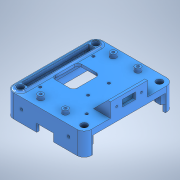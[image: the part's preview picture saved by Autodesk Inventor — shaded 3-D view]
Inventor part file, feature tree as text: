
AUTODESK INVENTOR PART (.ipt)
format: ipt  version: 2022 (Build 260153000, 153)  size: 752,640 bytes
history: native  units: mm
features: sketch x26, extrude x21, mirror x8, fillet x7, hole x5, plane x5
ambient origin geometry x8: Origin, YZ Plane, XZ Plane, XY Plane, X Axis, Y Axis, Z Axis, Center Point
bodies: Solid1 (feature_tree)
feature tree (72):
  extrude  "Extrusion1"  Depth=6.2mm
  extrude  "Extrusion2"  Depth=49.0mm
  extrude  "Extrusion3"  Depth=58.0mm
  extrude  "Extrusion4"  Depth=58.0mm
  extrude  "Extrusion5"  Depth=7.0mm
  hole  "Hole1"  [1 undecoded]
  extrude  "Extrusion6"  Depth=2.0mm TaperAngle=0.0deg
  extrude  "Extrusion8"  Depth=5.0mm
  extrude  "Extrusion12"  Depth=6.5mm
  extrude  "Extrusion13"  Depth=5.0mm
  extrude  "Extrusion14"  Depth=5.0mm TaperAngle=0.0deg
  extrude  "Extrusion15"  Depth=7.0mm
  fillet  "Fillet1"  Radius=17.0mm
  hole  "Hole2"  [1 undecoded]
  extrude  "Extrusion16"  Depth=2.0mm
  extrude  "Extrusion17"  Depth=9.525mm
  hole  "Hole3"  [1 undecoded]
  extrude  "Extrusion18"  Depth=3.0mm TaperAngle=0.0deg
  extrude  "Extrusion19"  Depth=11.0mm
  mirror  "Mirror4"
  extrude  "Extrusion20"  Depth=11.0mm
  hole  "Hole4"  [1 undecoded]
  plane  "Work Plane3"
  mirror  "Mirror5"
  hole  "Hole5"  [1 undecoded]
  extrude  "Extrusion21"  Depth=13.0mm
  plane  "Work Plane4"
  plane  "Work Plane5"
  mirror  "Mirror6"
  mirror  "Mirror7"
  fillet  "Fillet2"  Radius=6.0mm
  fillet  "Fillet3"  Radius=18.0mm
  extrude  "Extrusion22"  Depth=13.0mm
  fillet  "Fillet4"  Radius=13.0mm
  extrude  "Extrusion23"  Depth=2.0mm TaperAngle=0.0deg
  mirror  "Mirror8"
  mirror  "Mirror9"
  fillet  "Fillet5"  Radius=7.15mm
  fillet  "Fillet6"  Radius=7.15mm
  fillet  "Fillet7"  Radius=7.15mm
  extrude  "Extrusion24"  Depth=2.0mm TaperAngle=0.0deg
  extrude  "Extrusion25"  Depth=3.1mm
  mirror  "Mirror10"
  mirror  "Mirror11"
  sketch  "Sketch1"  dims[d0=6.2mm d1=6.2mm]
  sketch  "Sketch2"  dims[d2=6.2mm d3=49.0mm]
  sketch  "Sketch4"  dims[d4=58.0mm d5=6.2mm]
  sketch  "Sketch5"  dims[d6=58.0mm d7=49.0mm]
  sketch  "Sketch6"  dims[d8=10.0mm d9=0.0mm d10=7.0mm]
  sketch  "Sketch7"  dims[d11=7.0mm d12=7.0mm]
  sketch  "Sketch8"  dims[d13=7.0mm d14=2.0mm d15=0.0mm]
  sketch  "Sketch12"  dims[d19=1.0mm d20=5.0mm]
  sketch  "Sketch15"  dims[d21=52.0mm d22=6.5mm]
  sketch  "Sketch16"  dims[d23=2.0mm d24=0.0mm d31=5.0mm]
  sketch  "Sketch17"  dims[d32=5.0mm d33=5.0mm d34=0.0mm]
  sketch  "Sketch18"  dims[d35=20.5mm d36=7.0mm d37=17.0mm]
  sketch  "Sketch19"  dims[d39=5.5mm d40=0.0mm d41=16.0mm]
  sketch  "Sketch20"  dims[d42=2.0mm d43=6.0mm d44=4.0mm d45=2.0mm d46=90.0deg d47=8.0mm d48=20.594885mm d49=2.25mm]
  sketch  "Sketch21"  dims[d50=55.88mm d51=9.525mm]
  sketch  "Sketch22"  dims[d52=4.5mm d53=4.5mm]
  sketch  "Sketch23"  dims[d54=4.6mm d55=3.0mm d56=0.0mm]
  sketch  "Sketch24"  dims[d65=11.0mm d66=11.0mm]
  sketch  "Sketch25"  dims[d67=11.0mm d68=11.0mm]
  sketch  "Sketch26"  dims[d69=17.48mm d70=0.0mm d88=13.0mm]
  sketch  "Sketch27"  dims[d89=1.0mm d90=1.0mm]
  sketch  "Sketch28"  dims[d91=2.0mm d92=0.0mm d93=13.0mm d94=6.0mm d95=18.0mm]
  plane  "Work Plane6"
  plane  "Work Plane7"
  sketch  "Sketch29"  dims[d96=2.0mm d97=0.0mm d98=15.0mm d99=13.0mm]
  sketch  "Sketch30"  dims[d100=20.5mm d101=2.0mm d102=0.0mm d103=7.15mm d104=7.15mm d105=7.15mm]
  sketch  "Sketch32"  dims[d106=7.15mm d107=2.0mm d108=0.0mm]
  sketch  "Sketch34"  dims[d109=3.0mm d110=2.0mm d111=6.0mm d112=5.0mm d113=7.0mm d114=90.0deg d115=8.0mm d116=20.594885mm d117=3.1mm d118=1.0mm d119=2.0mm d120=0.0mm d121=0.0mm d122=14.036mm d123=14.036mm d124=12.1mm d125=12.1mm d126=6.0mm d127=6.0mm d128=6.0mm d129=6.0mm d130=4.0mm d131=0.0mm d132=2.0mm d133=6.0mm d134=5.0mm d135=7.0mm d136=90.0deg d137=8.0mm d138=20.594885mm d139=11.0mm d140=12.25mm d141=5.0mm d142=3.0mm d143=5.0mm d144=1.5mm d145=9.5mm d146=2.0mm d147=0.0mm d148=11.0mm d149=2.0mm d150=0.0mm d151=8.0mm d152=11.9mm d153=11.9mm d154=6.0mm d155=6.0mm d156=4.0mm d157=0.0mm d158=36.2mm d159=2.0mm d160=6.0mm d161=4.0mm d162=2.0mm d163=90.0deg d164=8.0mm d165=20.594885mm d166=2.0mm d167=6.0mm d168=4.0mm d169=2.0mm d170=90.0deg d171=8.0mm d172=20.594885mm d173=0.0mm d174=0.0mm d175=7.0mm d176=2.0mm d177=2.0mm d178=0.0mm d179=3.0mm d180=6.0mm d181=2.0mm d182=0.0mm d183=4.0mm d184=2.0mm d185=2.0mm d186=2.0mm d187=0.0mm d188=8.0mm d189=8.0mm d190=7.3mm d191=2.0mm d192=0.0mm]
note: 5 required parameter values undecoded (feature->parameter linkage not recoverable at this tier; creation-order binding heuristic only, values carry confidence <= 0.55)
